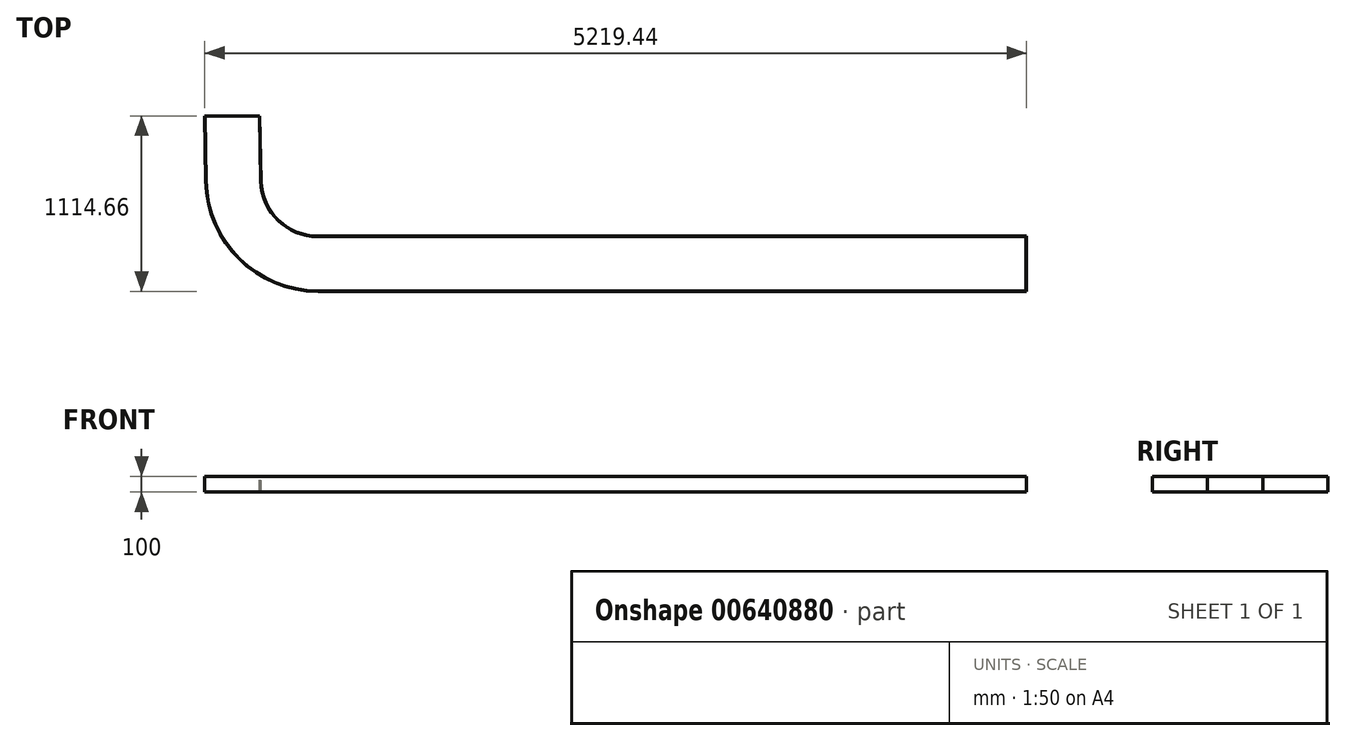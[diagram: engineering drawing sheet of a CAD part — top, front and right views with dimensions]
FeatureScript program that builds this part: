
annotation { "Feature Type Name" : "Feature", "Feature Type Description" : "" }
export const myFeature = defineFeature(function(context is Context, id is Id, definition is map)
    precondition{}
    {
        {
            var Q0;
            Q0=qCreatedBy(makeId("Top.planeOp"),FACE);
            var sketch = newSketch(context, id + "F0", { "sketchPlane" : qUnion([Q0])});
            skLineSegment(sketch, "E0.bottom", {"start": v(-2250, -350) * mm, "end": v(2250, -350) * mm});
            skLineSegment(sketch, "E0.top", {"start": v(-2250, -700) * mm, "end": v(2250, -700) * mm});
            skLineSegment(sketch, "E0.right", {"start": v(2250, -350) * mm, "end": v(2250, -700) * mm});
            skLineSegment(sketch, "E1", {"start": v(0, 1876.7) * mm, "end": v(0, -1907.39) * mm, "construction": true});
            skLineSegment(sketch, "E2", {"start": v(-1228.23, 0) * mm, "end": v(2971.02, 0) * mm, "construction": true});
            skArc(sketch, "E3", {"start": v(-2962.25, 0) * mm, "mid": v(-2749.32, -495.7) * mm, "end": v(-2250, -700) * mm});
            skArc(sketch, "E4", {"start": v(-2612.25, 0) * mm, "mid": v(-2501.86, -248.2) * mm, "end": v(-2250, -350) * mm});
            skLineSegment(sketch, "E5", {"start": v(-2962.25, 0) * mm, "end": v(-2969.44, 414.66) * mm});
            skLineSegment(sketch, "E6", {"start": v(-2969.44, 414.66) * mm, "end": v(-2619.44, 414.66) * mm});
            skLineSegment(sketch, "E7", {"start": v(-2619.44, 414.66) * mm, "end": v(-2612.25, 0) * mm});
            skSolve(sketch);
        }
        {
            var Q0;
            Q0 = qSketchRegion(id + "F0", true);
            extrude(context, id + "F1", {"entities" : qUnion([Q0]), "oppositeDirection" : true, "depth" : 100 * mm, "offsetDistance" : 25.4 * mm});
        }
        {
            var Q0;
            Q0=makeQuery(id+"F1.opExtrude","CAP_FACE",FACE,{"disambiguationData":[OSD([sQuery(id+"F0.wireOp",EDGE,"E0.bottom"),sQuery(id+"F0.wireOp",EDGE,"E0.top"),sQuery(id+"F0.wireOp",EDGE,"E0.right"),sQuery(id+"F0.wireOp",EDGE,"E3"),sQuery(id+"F0.wireOp",EDGE,"E4"),sQuery(id+"F0.wireOp",EDGE,"E5"),sQuery(id+"F0.wireOp",EDGE,"E6"),sQuery(id+"F0.wireOp",EDGE,"E7")])],"isStart":true});
            shell(context, id + "F2", {"entities" : qUnion([Q0]), "thickness" : 2.54 * mm});
        }
    });
